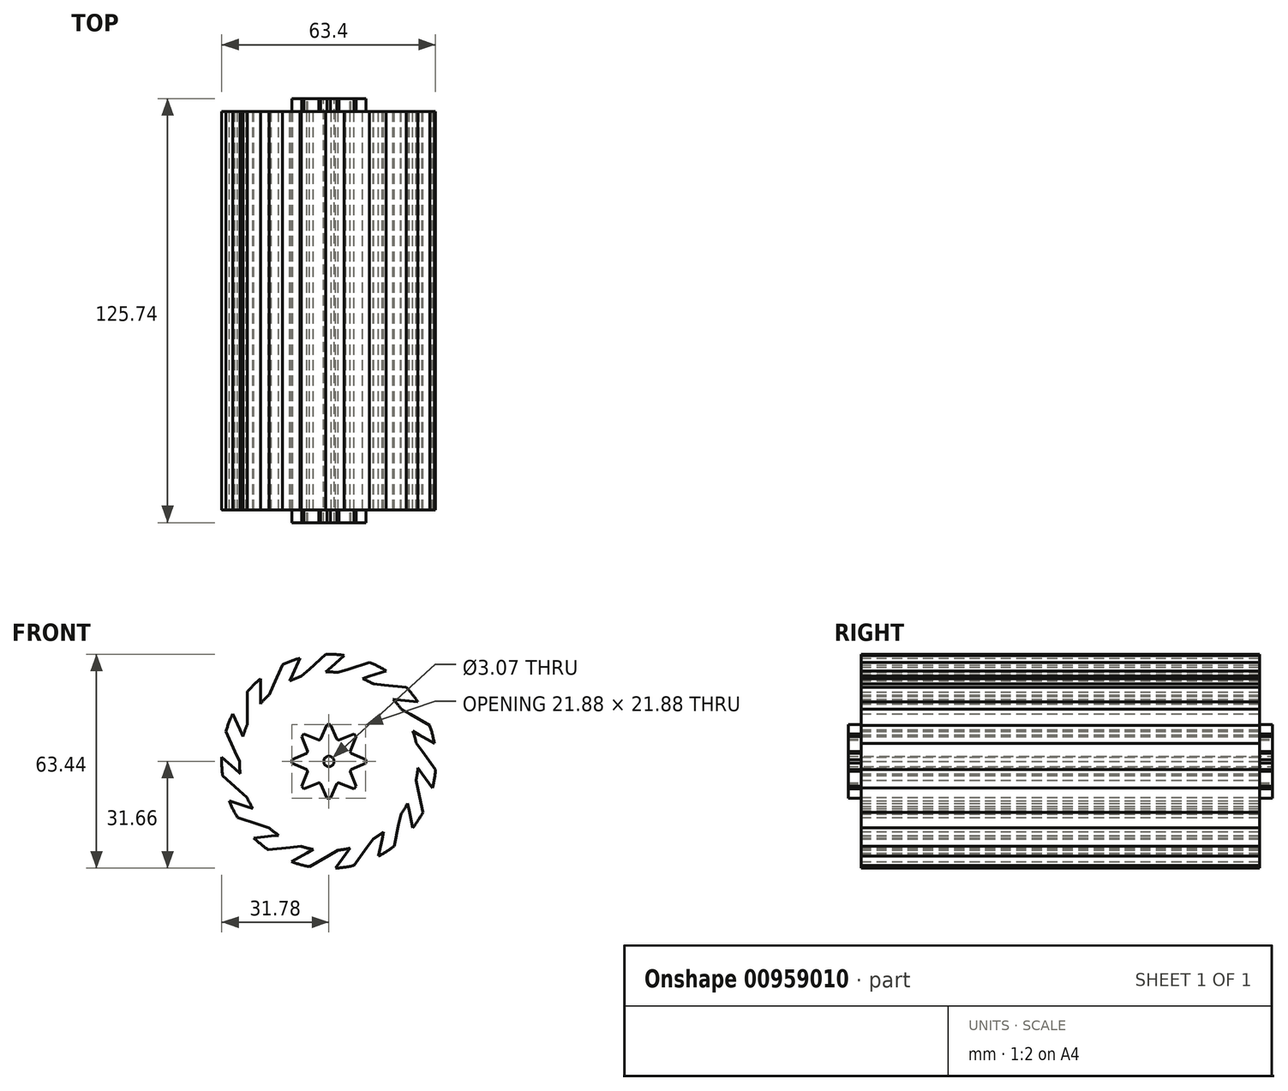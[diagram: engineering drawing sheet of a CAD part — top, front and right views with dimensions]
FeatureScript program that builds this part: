
annotation { "Feature Type Name" : "Feature", "Feature Type Description" : "" }
export const myFeature = defineFeature(function(context is Context, id is Id, definition is map)
    precondition{}
    {
        {
            var Q0;
            Q0=qCreatedBy(makeId("Front.planeOp"),FACE);
            var sketch = newSketch(context, id + "F0", { "sketchPlane" : qUnion([Q0])});
            skCircle(sketch, "E0", {"center": v(-0.03, 0.03) * mm, "radius": 31.75 * mm});
            skCircle(sketch, "E1", {"center": v(-0.03, 0.03) * mm, "radius": 25.4 * mm});
            skLineSegment(sketch, "E2", {"start": v(5.81, 27.35) * mm, "end": v(12.03, 29.4) * mm});
            skLineSegment(sketch, "E3", {"start": v(12.02, 25.23) * mm, "end": v(16.95, 26.86) * mm});
            skLineSegment(sketch, "E4.1.0", {"start": v(0.72, 27.96) * mm, "end": v(4.57, 31.44) * mm});
            skLineSegment(sketch, "E4.1.1", {"start": v(-5.8, 27.37) * mm, "end": v(-0.95, 31.76) * mm});
            skLineSegment(sketch, "E4.2.0", {"start": v(-10.7, 25.85) * mm, "end": v(-8.6, 30.6) * mm});
            skLineSegment(sketch, "E4.2.1", {"start": v(-16.43, 22.65) * mm, "end": v(-13.78, 28.65) * mm});
            skLineSegment(sketch, "E4.3.0", {"start": v(-20.28, 19.28) * mm, "end": v(-20.3, 24.47) * mm});
            skLineSegment(sketch, "E4.3.1", {"start": v(-24.21, 14.03) * mm, "end": v(-24.23, 20.58) * mm});
            skLineSegment(sketch, "E4.4.0", {"start": v(-26.36, 9.38) * mm, "end": v(-28.49, 14.11) * mm});
            skLineSegment(sketch, "E4.4.1", {"start": v(-27.82, 2.99) * mm, "end": v(-30.5, 8.96) * mm});
            skLineSegment(sketch, "E4.5.0", {"start": v(-27.9, -2.14) * mm, "end": v(-31.76, 1.32) * mm});
            skLineSegment(sketch, "E4.5.1", {"start": v(-26.62, -8.57) * mm, "end": v(-31.5, -4.2) * mm});
            skLineSegment(sketch, "E4.6.0", {"start": v(-24.6, -13.28) * mm, "end": v(-29.54, -11.7) * mm});
            skLineSegment(sketch, "E4.6.1", {"start": v(-20.82, -18.64) * mm, "end": v(-27.06, -16.64) * mm});
            skLineSegment(sketch, "E4.7.0", {"start": v(-17.07, -22.12) * mm, "end": v(-22.22, -22.68) * mm});
            skLineSegment(sketch, "E4.7.1", {"start": v(-11.43, -25.48) * mm, "end": v(-17.95, -26.19) * mm});
            skLineSegment(sketch, "E4.8.0", {"start": v(-6.58, -27.13) * mm, "end": v(-11.07, -29.74) * mm});
            skLineSegment(sketch, "E4.8.1", {"start": v(-0.07, -27.91) * mm, "end": v(-5.73, -31.2) * mm});
            skLineSegment(sketch, "E4.9.0", {"start": v(5.03, -27.45) * mm, "end": v(2, -31.66) * mm});
            skLineSegment(sketch, "E4.9.1", {"start": v(11.3, -25.51) * mm, "end": v(7.46, -30.82) * mm});
            skLineSegment(sketch, "E4.10.0", {"start": v(15.77, -23.01) * mm, "end": v(14.7, -28.1) * mm});
            skLineSegment(sketch, "E4.10.1", {"start": v(20.7, -18.7) * mm, "end": v(19.36, -25.1) * mm});
            skLineSegment(sketch, "E4.11.0", {"start": v(23.77, -14.6) * mm, "end": v(24.87, -19.66) * mm});
            skLineSegment(sketch, "E4.11.1", {"start": v(26.53, -8.64) * mm, "end": v(27.9, -15.04) * mm});
            skLineSegment(sketch, "E4.12.0", {"start": v(27.66, -3.65) * mm, "end": v(30.73, -7.83) * mm});
            skLineSegment(sketch, "E4.12.1", {"start": v(27.76, 2.91) * mm, "end": v(31.62, -2.37) * mm});
            skLineSegment(sketch, "E4.13.0", {"start": v(26.76, 7.94) * mm, "end": v(31.26, 5.36) * mm});
            skLineSegment(sketch, "E4.13.1", {"start": v(24.18, 13.97) * mm, "end": v(29.86, 10.7) * mm});
            skLineSegment(sketch, "E4.14.0", {"start": v(21.23, 18.15) * mm, "end": v(26.4, 17.63) * mm});
            skLineSegment(sketch, "E4.14.1", {"start": v(16.42, 22.6) * mm, "end": v(22.93, 21.95) * mm});
            skCircle(sketch, "E5", {"center": v(-0.03, 0.03) * mm, "radius": 24.13 * mm});
            skPoint(sketch, "E6.orphan", {"position": v(-10.37, 23.23) * mm});
            skPoint(sketch, "E7.orphan", {"position": v(-2.17, 25.34) * mm});
            skPoint(sketch, "E8.orphan", {"position": v(-0.03, 25.43) * mm});
            skPoint(sketch, "E9.orphan", {"position": v(8.31, 24.02) * mm});
            skPoint(sketch, "E10.orphan", {"position": v(10.3, 23.23) * mm});
            skPoint(sketch, "E11.orphan", {"position": v(17.35, 18.55) * mm});
            skPoint(sketch, "E12.orphan", {"position": v(18.84, 17.02) * mm});
            skPoint(sketch, "E13.orphan", {"position": v(23.38, 9.88) * mm});
            skPoint(sketch, "E14.orphan", {"position": v(24.12, 7.88) * mm});
            skPoint(sketch, "E15.orphan", {"position": v(25.36, -0.5) * mm});
            skPoint(sketch, "E16.orphan", {"position": v(25.23, -2.63) * mm});
            skPoint(sketch, "E17.orphan", {"position": v(22.95, -10.78) * mm});
            skPoint(sketch, "E18.orphan", {"position": v(21.96, -12.67) * mm});
            skPoint(sketch, "E19.orphan", {"position": v(16.57, -19.2) * mm});
            skPoint(sketch, "E20.orphan", {"position": v(14.9, -20.52) * mm});
            skPoint(sketch, "E21.orphan", {"position": v(7.31, -24.29) * mm});
            skPoint(sketch, "E22.orphan", {"position": v(5.25, -24.82) * mm});
            skPoint(sketch, "E23.orphan", {"position": v(-3.21, -25.17) * mm});
            skPoint(sketch, "E24.orphan", {"position": v(-5.32, -24.82) * mm});
            skPoint(sketch, "E25.orphan", {"position": v(-13.19, -21.7) * mm});
            skPoint(sketch, "E26.orphan", {"position": v(-14.96, -20.52) * mm});
            skPoint(sketch, "E27.orphan", {"position": v(-20.89, -14.47) * mm});
            skPoint(sketch, "E28.orphan", {"position": v(-22.03, -12.67) * mm});
            skPoint(sketch, "E29.orphan", {"position": v(-24.98, -4.74) * mm});
            skPoint(sketch, "E30.orphan", {"position": v(-25.3, -2.63) * mm});
            skPoint(sketch, "E31.orphan", {"position": v(-24.77, 5.82) * mm});
            skPoint(sketch, "E32.orphan", {"position": v(-24.2, 7.88) * mm});
            skPoint(sketch, "E33.orphan", {"position": v(-20.27, 15.38) * mm});
            skPoint(sketch, "E34.orphan", {"position": v(-18.91, 17.02) * mm});
            skPoint(sketch, "E35.orphan", {"position": v(-12.28, 22.28) * mm});
            skCircle(sketch, "E36", {"center": v(-0.03, 0.03) * mm, "radius": 26.5 * mm});
            skLineSegment(sketch, "E37", {"start": v(16.42, 22.6) * mm, "end": v(13.25, 22.95) * mm});
            skLineSegment(sketch, "E38", {"start": v(21.23, 18.15) * mm, "end": v(19.05, 18.4) * mm});
            skLineSegment(sketch, "E39.1.0", {"start": v(5.81, 27.35) * mm, "end": v(2.78, 26.37) * mm});
            skLineSegment(sketch, "E39.1.1", {"start": v(12.02, 25.23) * mm, "end": v(9.93, 24.57) * mm});
            skLineSegment(sketch, "E39.2.0", {"start": v(-5.8, 27.37) * mm, "end": v(-8.18, 25.24) * mm});
            skLineSegment(sketch, "E39.2.1", {"start": v(0.72, 27.96) * mm, "end": v(-0.92, 26.5) * mm});
            skLineSegment(sketch, "E39.3.0", {"start": v(-16.43, 22.65) * mm, "end": v(-17.73, 19.75) * mm});
            skLineSegment(sketch, "E39.3.1", {"start": v(-10.7, 25.85) * mm, "end": v(-11.6, 23.86) * mm});
            skLineSegment(sketch, "E39.4.0", {"start": v(-24.21, 14.03) * mm, "end": v(-24.22, 10.84) * mm});
            skLineSegment(sketch, "E39.4.1", {"start": v(-20.28, 19.28) * mm, "end": v(-20.3, 17.09) * mm});
            skLineSegment(sketch, "E39.5.0", {"start": v(-27.82, 2.99) * mm, "end": v(-26.53, 0.07) * mm});
            skLineSegment(sketch, "E39.5.1", {"start": v(-26.36, 9.38) * mm, "end": v(-25.49, 7.37) * mm});
            skLineSegment(sketch, "E39.6.0", {"start": v(-26.62, -8.57) * mm, "end": v(-24.25, -10.7) * mm});
            skLineSegment(sketch, "E39.6.1", {"start": v(-27.9, -2.14) * mm, "end": v(-26.27, -3.62) * mm});
            skLineSegment(sketch, "E39.7.0", {"start": v(-20.82, -18.64) * mm, "end": v(-17.8, -19.63) * mm});
            skLineSegment(sketch, "E39.7.1", {"start": v(-24.6, -13.28) * mm, "end": v(-22.52, -13.97) * mm});
            skLineSegment(sketch, "E39.8.0", {"start": v(-11.43, -25.48) * mm, "end": v(-8.26, -25.15) * mm});
            skLineSegment(sketch, "E39.8.1", {"start": v(-17.07, -22.12) * mm, "end": v(-14.88, -21.9) * mm});
            skLineSegment(sketch, "E39.9.0", {"start": v(-0.07, -27.91) * mm, "end": v(2.69, -26.32) * mm});
            skLineSegment(sketch, "E39.9.1", {"start": v(-6.58, -27.13) * mm, "end": v(-4.68, -26.05) * mm});
            skLineSegment(sketch, "E39.10.0", {"start": v(11.3, -25.51) * mm, "end": v(13.17, -22.94) * mm});
            skLineSegment(sketch, "E39.10.1", {"start": v(5.03, -27.45) * mm, "end": v(6.33, -25.69) * mm});
            skLineSegment(sketch, "E39.11.0", {"start": v(20.7, -18.7) * mm, "end": v(21.37, -15.58) * mm});
            skLineSegment(sketch, "E39.11.1", {"start": v(15.77, -23.01) * mm, "end": v(16.24, -20.87) * mm});
            skLineSegment(sketch, "E39.12.0", {"start": v(26.53, -8.64) * mm, "end": v(25.87, -5.52) * mm});
            skLineSegment(sketch, "E39.12.1", {"start": v(23.77, -14.6) * mm, "end": v(23.34, -12.45) * mm});
            skLineSegment(sketch, "E39.13.0", {"start": v(27.76, 2.91) * mm, "end": v(25.89, 5.5) * mm});
            skLineSegment(sketch, "E39.13.1", {"start": v(27.66, -3.65) * mm, "end": v(26.39, -1.86) * mm});
            skLineSegment(sketch, "E39.14.0", {"start": v(24.18, 13.97) * mm, "end": v(21.42, 15.56) * mm});
            skLineSegment(sketch, "E39.14.1", {"start": v(26.76, 7.94) * mm, "end": v(24.87, 9.05) * mm});
            skCircle(sketch, "E40", {"center": v(0, 0) * mm, "radius": 3.56 * mm});
            skSolve(sketch);
        }
        {
            var Q0;
            {var subQ4=sQuery(id+"F0.wireOp",EDGE,"E4.1.0");Q0=makeQuery(id+"F0.imprint","IMPRINT",FACE,{"disambiguationData":[TD([[makeQuery(id+"F0.imprint","IMPRINT",EDGE,{"derivedFrom":subQ4}),1.0]])]});}
            var Q1;
            {var subQ4=sQuery(id+"F0.wireOp",EDGE,"E2");Q1=makeQuery(id+"F0.imprint","IMPRINT",FACE,{"disambiguationData":[TD([[makeQuery(id+"F0.imprint","IMPRINT",EDGE,{"derivedFrom":subQ4}),-1.0]])]});}
            var Q2;
            {var subQ4=sQuery(id+"F0.wireOp",EDGE,"E4.14.0");Q2=makeQuery(id+"F0.imprint","IMPRINT",FACE,{"disambiguationData":[TD([[makeQuery(id+"F0.imprint","IMPRINT",EDGE,{"derivedFrom":subQ4}),1.0]])]});}
            var Q3;
            {var subQ4=sQuery(id+"F0.wireOp",EDGE,"E4.13.0");Q3=makeQuery(id+"F0.imprint","IMPRINT",FACE,{"disambiguationData":[TD([[makeQuery(id+"F0.imprint","IMPRINT",EDGE,{"derivedFrom":subQ4}),1.0]])]});}
            var Q4;
            {var subQ4=sQuery(id+"F0.wireOp",EDGE,"E4.12.0");Q4=makeQuery(id+"F0.imprint","IMPRINT",FACE,{"disambiguationData":[TD([[makeQuery(id+"F0.imprint","IMPRINT",EDGE,{"derivedFrom":subQ4}),1.0]])]});}
            var Q5;
            {var subQ4=sQuery(id+"F0.wireOp",EDGE,"E4.11.0");Q5=makeQuery(id+"F0.imprint","IMPRINT",FACE,{"disambiguationData":[TD([[makeQuery(id+"F0.imprint","IMPRINT",EDGE,{"derivedFrom":subQ4}),1.0]])]});}
            var Q6;
            {var subQ4=sQuery(id+"F0.wireOp",EDGE,"E4.10.0");Q6=makeQuery(id+"F0.imprint","IMPRINT",FACE,{"disambiguationData":[TD([[makeQuery(id+"F0.imprint","IMPRINT",EDGE,{"derivedFrom":subQ4}),1.0]])]});}
            var Q7;
            {var subQ4=sQuery(id+"F0.wireOp",EDGE,"E4.9.0");Q7=makeQuery(id+"F0.imprint","IMPRINT",FACE,{"disambiguationData":[TD([[makeQuery(id+"F0.imprint","IMPRINT",EDGE,{"derivedFrom":subQ4}),1.0]])]});}
            var Q8;
            {var subQ4=sQuery(id+"F0.wireOp",EDGE,"E4.8.0");Q8=makeQuery(id+"F0.imprint","IMPRINT",FACE,{"disambiguationData":[TD([[makeQuery(id+"F0.imprint","IMPRINT",EDGE,{"derivedFrom":subQ4}),1.0]])]});}
            var Q9;
            {var subQ4=sQuery(id+"F0.wireOp",EDGE,"E4.7.0");Q9=makeQuery(id+"F0.imprint","IMPRINT",FACE,{"disambiguationData":[TD([[makeQuery(id+"F0.imprint","IMPRINT",EDGE,{"derivedFrom":subQ4}),1.0]])]});}
            var Q10;
            {var subQ4=sQuery(id+"F0.wireOp",EDGE,"E4.6.0");Q10=makeQuery(id+"F0.imprint","IMPRINT",FACE,{"disambiguationData":[TD([[makeQuery(id+"F0.imprint","IMPRINT",EDGE,{"derivedFrom":subQ4}),1.0]])]});}
            var Q11;
            {var subQ4=sQuery(id+"F0.wireOp",EDGE,"E4.5.0");Q11=makeQuery(id+"F0.imprint","IMPRINT",FACE,{"disambiguationData":[TD([[makeQuery(id+"F0.imprint","IMPRINT",EDGE,{"derivedFrom":subQ4}),1.0]])]});}
            var Q12;
            {var subQ4=sQuery(id+"F0.wireOp",EDGE,"E4.4.0");Q12=makeQuery(id+"F0.imprint","IMPRINT",FACE,{"disambiguationData":[TD([[makeQuery(id+"F0.imprint","IMPRINT",EDGE,{"derivedFrom":subQ4}),1.0]])]});}
            var Q13;
            {var subQ4=sQuery(id+"F0.wireOp",EDGE,"E4.3.0");Q13=makeQuery(id+"F0.imprint","IMPRINT",FACE,{"disambiguationData":[TD([[makeQuery(id+"F0.imprint","IMPRINT",EDGE,{"derivedFrom":subQ4}),1.0]])]});}
            var Q14;
            {var subQ4=sQuery(id+"F0.wireOp",EDGE,"E4.2.0");Q14=makeQuery(id+"F0.imprint","IMPRINT",FACE,{"disambiguationData":[TD([[makeQuery(id+"F0.imprint","IMPRINT",EDGE,{"derivedFrom":subQ4}),1.0]])]});}
            var Q15;
            Q15=makeQuery(id+"F0.imprint","IMPRINT",FACE,{"disambiguationData":[TD([[makeQuery(id+"F0.imprint","IMPRINT",EDGE,{"derivedFrom":sQuery(id+"F0.wireOp",EDGE,"E1")}),-1.0]])]});
            var Q16;
            Q16=makeQuery(id+"F0.imprint","IMPRINT",FACE,{"disambiguationData":[TD([[makeQuery(id+"F0.imprint","IMPRINT",EDGE,{"derivedFrom":sQuery(id+"F0.wireOp",EDGE,"E1")}),1.0]])]});
            var Q17;
            Q17=makeQuery(id+"F0.imprint","IMPRINT",FACE,{"disambiguationData":[TD([[makeQuery(id+"F0.imprint","IMPRINT",EDGE,{"derivedFrom":sQuery(id+"F0.wireOp",EDGE,"E5")}),1.0]])]});
            extrude(context, id + "F1", {"entities" : qUnion([Q0, Q1, Q2, Q3, Q4, Q5, Q6, Q7, Q8, Q9, Q10, Q11, Q12, Q13, Q14, Q15, Q16, Q17]), "endBound" : BoundingType.SYMMETRIC, "depth" : 118.11 * mm, "offsetDistance" : 25.4 * mm});
        }
        {
            var Q0;
            Q0=makeQuery(id+"F0.imprint","IMPRINT",FACE,{"disambiguationData":[TD([[makeQuery(id+"F0.imprint","IMPRINT",EDGE,{"derivedFrom":sQuery(id+"F0.wireOp",EDGE,"E40")}),1.0]])]});
            extrude(context, id + "F2", {"entities" : qUnion([Q0]), "operationType" : NewBodyOperationType.ADD, "endBound" : BoundingType.SYMMETRIC, "depth" : 125.73 * mm, "offsetDistance" : 25.4 * mm});
        }
        {
            var Q0;
            Q0=makeQuery(id+"F2.opExtrude","CAP_FACE",FACE,{"disambiguationData":[OSD([sQuery(id+"F0.wireOp",EDGE,"E40")])],"isStart":true});
            var sketch = newSketch(context, id + "F3", { "sketchPlane" : qUnion([Q0])});
            skCircle(sketch, "E41", {"center": v(0, 0) * mm, "radius": 6.99 * mm});
            skLineSegment(sketch, "E42", {"start": v(0, 6.98) * mm, "end": v(0, 10.94) * mm});
            skLineSegment(sketch, "E43", {"start": v(-2.41, 6.55) * mm, "end": v(-0.5, 10.94) * mm});
            skLineSegment(sketch, "E44", {"start": v(-0.5, 10.94) * mm, "end": v(0.5, 10.94) * mm});
            skLineSegment(sketch, "E45", {"start": v(2.4, 6.56) * mm, "end": v(0.5, 10.94) * mm});
            skLineSegment(sketch, "E46.1.0", {"start": v(-2.94, 6.34) * mm, "end": v(-7.39, 8.08) * mm});
            skLineSegment(sketch, "E46.1.1", {"start": v(-4.94, 4.94) * mm, "end": v(-7.74, 7.73) * mm});
            skLineSegment(sketch, "E46.1.2", {"start": v(-6.34, 2.93) * mm, "end": v(-8.09, 7.38) * mm});
            skLineSegment(sketch, "E46.1.3", {"start": v(-8.09, 7.38) * mm, "end": v(-7.39, 8.08) * mm});
            skLineSegment(sketch, "E46.2.0", {"start": v(-6.56, 2.4) * mm, "end": v(-10.94, 0.5) * mm});
            skLineSegment(sketch, "E46.2.1", {"start": v(-6.98, 0) * mm, "end": v(-10.94, 0) * mm});
            skLineSegment(sketch, "E46.2.2", {"start": v(-6.55, -2.41) * mm, "end": v(-10.94, -0.5) * mm});
            skLineSegment(sketch, "E46.2.3", {"start": v(-10.94, -0.5) * mm, "end": v(-10.94, 0.5) * mm});
            skLineSegment(sketch, "E46.3.0", {"start": v(-6.34, -2.94) * mm, "end": v(-8.08, -7.39) * mm});
            skLineSegment(sketch, "E46.3.1", {"start": v(-4.94, -4.94) * mm, "end": v(-7.73, -7.74) * mm});
            skLineSegment(sketch, "E46.3.2", {"start": v(-2.93, -6.34) * mm, "end": v(-7.38, -8.09) * mm});
            skLineSegment(sketch, "E46.3.3", {"start": v(-7.38, -8.09) * mm, "end": v(-8.08, -7.39) * mm});
            skLineSegment(sketch, "E46.4.0", {"start": v(-2.4, -6.56) * mm, "end": v(-0.5, -10.94) * mm});
            skLineSegment(sketch, "E46.4.1", {"start": v(0, -6.98) * mm, "end": v(0, -10.94) * mm});
            skLineSegment(sketch, "E46.4.2", {"start": v(2.41, -6.55) * mm, "end": v(0.5, -10.94) * mm});
            skLineSegment(sketch, "E46.4.3", {"start": v(0.5, -10.94) * mm, "end": v(-0.5, -10.94) * mm});
            skLineSegment(sketch, "E46.5.0", {"start": v(2.94, -6.34) * mm, "end": v(7.39, -8.08) * mm});
            skLineSegment(sketch, "E46.5.1", {"start": v(4.94, -4.94) * mm, "end": v(7.74, -7.73) * mm});
            skLineSegment(sketch, "E46.5.2", {"start": v(6.34, -2.93) * mm, "end": v(8.09, -7.38) * mm});
            skLineSegment(sketch, "E46.5.3", {"start": v(8.09, -7.38) * mm, "end": v(7.39, -8.08) * mm});
            skLineSegment(sketch, "E46.6.0", {"start": v(6.56, -2.4) * mm, "end": v(10.94, -0.5) * mm});
            skLineSegment(sketch, "E46.6.1", {"start": v(6.98, 0) * mm, "end": v(10.94, 0) * mm});
            skLineSegment(sketch, "E46.6.2", {"start": v(6.55, 2.41) * mm, "end": v(10.94, 0.5) * mm});
            skLineSegment(sketch, "E46.6.3", {"start": v(10.94, 0.5) * mm, "end": v(10.94, -0.5) * mm});
            skLineSegment(sketch, "E46.7.0", {"start": v(6.34, 2.94) * mm, "end": v(8.08, 7.39) * mm});
            skLineSegment(sketch, "E46.7.1", {"start": v(4.94, 4.94) * mm, "end": v(7.73, 7.74) * mm});
            skLineSegment(sketch, "E46.7.2", {"start": v(2.93, 6.34) * mm, "end": v(7.38, 8.09) * mm});
            skLineSegment(sketch, "E46.7.3", {"start": v(7.38, 8.09) * mm, "end": v(8.08, 7.39) * mm});
            skCircle(sketch, "E47", {"center": v(0, 0) * mm, "radius": 1.54 * mm});
            skSolve(sketch);
        }
        {
            var Q0;
            Q0 = qSketchRegion(id + "F3", true);
            extrude(context, id + "F4", {"entities" : qUnion([Q0]), "operationType" : NewBodyOperationType.ADD, "oppositeDirection" : true, "depth" : 125.73 * mm, "offsetDistance" : 25.4 * mm});
        }
        {
            var Q0;
            Q0=makeQuery(id+"F3.imprint","IMPRINT",FACE,{"disambiguationData":[TD([[makeQuery(id+"F3.imprint","IMPRINT",EDGE,{"derivedFrom":sQuery(id+"F3.wireOp",EDGE,"E47")}),1.0]])]});
            extrude(context, id + "F5", {"entities" : qUnion([Q0]), "operationType" : NewBodyOperationType.REMOVE, "endBound" : BoundingType.THROUGH_ALL, "oppositeDirection" : true, "depth" : 25.4 * mm, "offsetDistance" : 25.4 * mm});
        }
    });
